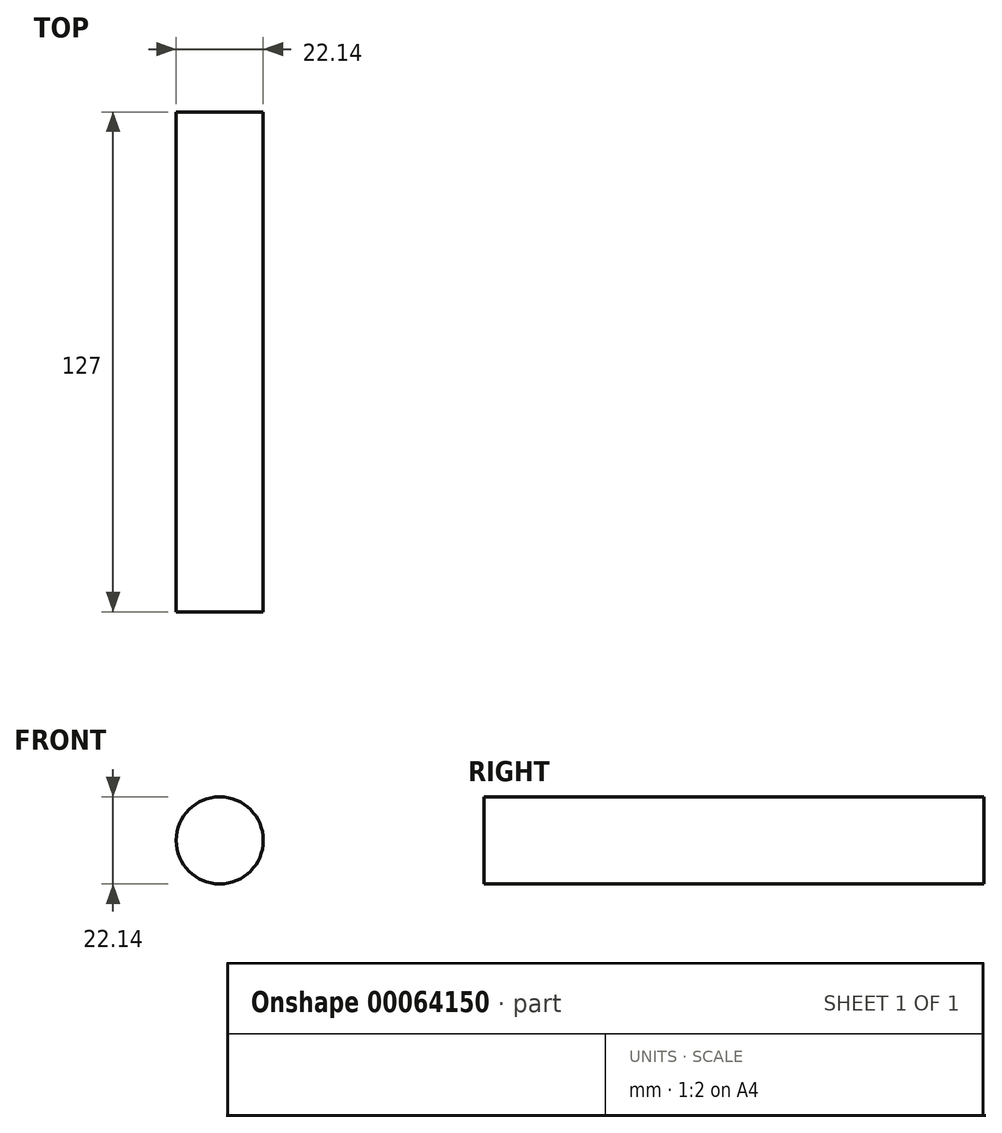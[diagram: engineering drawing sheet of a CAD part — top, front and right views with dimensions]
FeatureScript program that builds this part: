
annotation { "Feature Type Name" : "Feature", "Feature Type Description" : "" }
export const myFeature = defineFeature(function(context is Context, id is Id, definition is map)
    precondition{}
    {
        {
            var Q0;
            Q0=qCreatedBy(makeId("Front.planeOp"),FACE);
            var sketch = newSketch(context, id + "F0", { "sketchPlane" : qUnion([Q0])});
            skCircle(sketch, "E0", {"center": v(0, 0) * mm, "radius": 9.52 * mm});
            skSolve(sketch);
        }
        {
            var Q0;
            Q0=makeQuery(id+"F0.imprint","IMPRINT",FACE,{"disambiguationData":[TD([[makeQuery(id+"F0.imprint","IMPRINT",EDGE,{"derivedFrom":sQuery(id+"F0.wireOp",EDGE,"E0")}),1.0]])]});
            extrude(context, id + "F1", {"entities" : qUnion([Q0]), "depth" : 101.6 * mm});
        }
        {
            var Q0;
            Q0=makeQuery(id+"F1.opExtrude","SWEPT_BODY",BODY,{"disambiguationData":[OSD([sQuery(id+"F0.wireOp",EDGE,"E0")])]});
            deleteBodies(context, id + "F2", {"entities" : qUnion([Q0])});
        }
        {
            var Q0;
            Q0=qCreatedBy(makeId("Front.planeOp"),FACE);
            var sketch = newSketch(context, id + "F3", { "sketchPlane" : qUnion([Q0])});
            skCircle(sketch, "E1", {"center": v(0, 0) * mm, "radius": 11.07 * mm});
            skSolve(sketch);
        }
        {
            var Q0;
            Q0=makeQuery(id+"F3.imprint","IMPRINT",FACE,{"disambiguationData":[TD([[makeQuery(id+"F3.imprint","IMPRINT",EDGE,{"derivedFrom":sQuery(id+"F3.wireOp",EDGE,"E1")}),1.0]])]});
            extrude(context, id + "F4", {"entities" : qUnion([Q0]), "depth" : 127 * mm});
        }
    });
